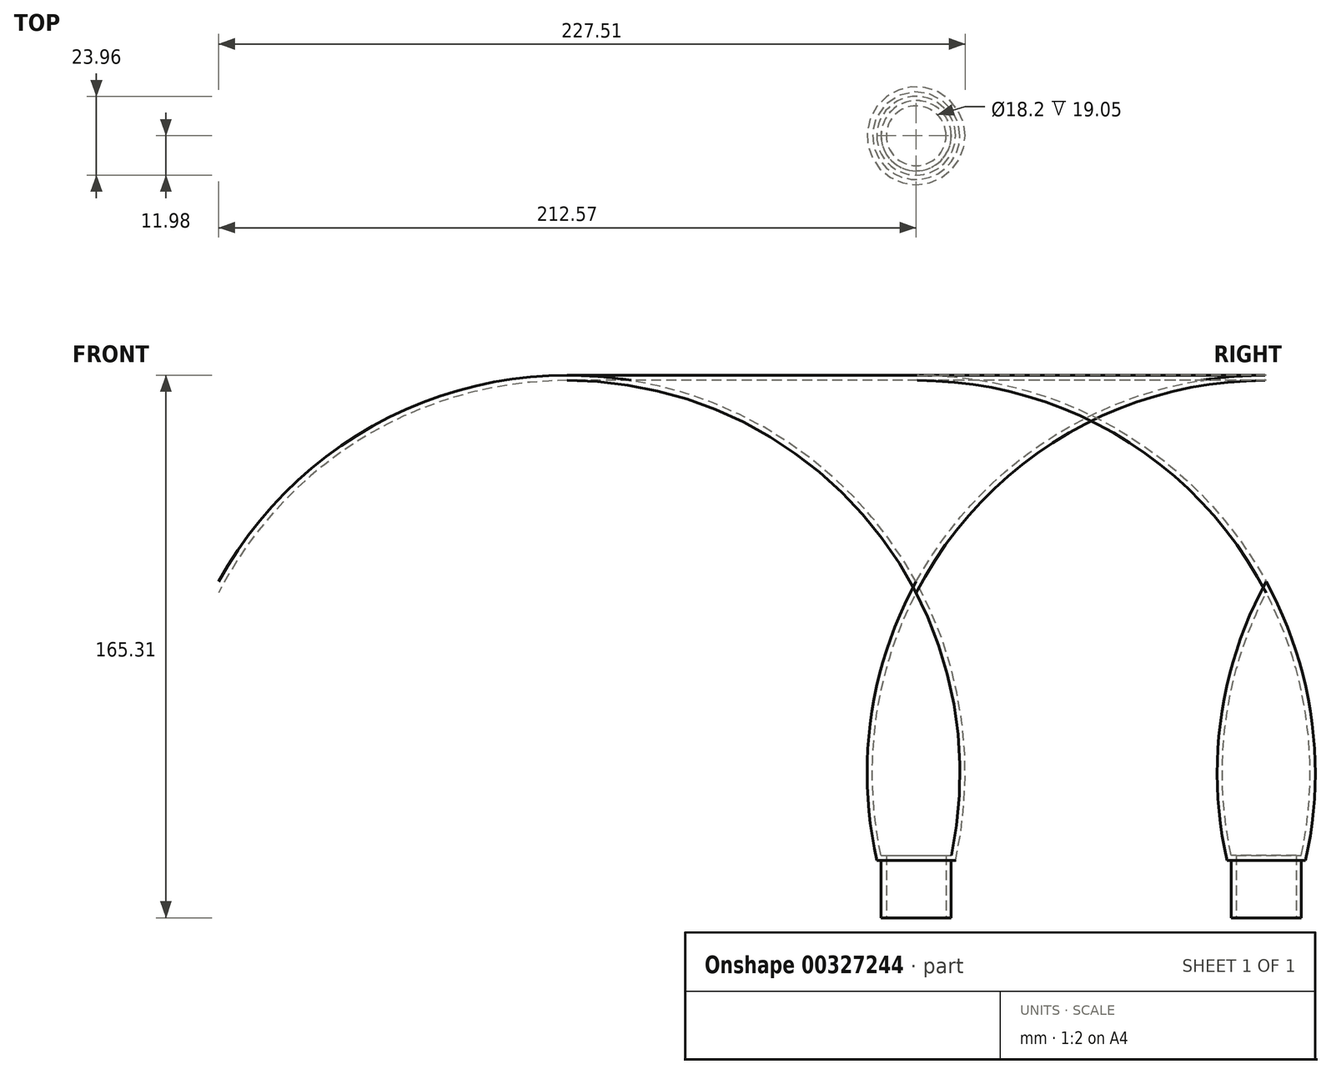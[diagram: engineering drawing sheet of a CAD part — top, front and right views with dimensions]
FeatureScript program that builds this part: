
annotation { "Feature Type Name" : "Feature", "Feature Type Description" : "" }
export const myFeature = defineFeature(function(context is Context, id is Id, definition is map)
    precondition{}
    {
        {
            var Q0;
            Q0=qCreatedBy(makeId("Front.planeOp"),FACE);
            var sketch = newSketch(context, id + "F0", { "sketchPlane" : qUnion([Q0])});
            skLineSegment(sketch, "E0", {"start": v(0, 0) * mm, "end": v(0, 99) * mm});
            skLineSegment(sketch, "E1", {"start": v(0, 0) * mm, "end": v(9.1, 0) * mm});
            skLineSegment(sketch, "E2", {"start": v(9.1, 0) * mm, "end": v(9.1, 19.05) * mm});
            skLineSegment(sketch, "E3", {"start": v(9.1, 19.05) * mm, "end": v(10.7, 19.05) * mm});
            skArc(sketch, "E4", {"start": v(10.7, 19.05) * mm, "mid": v(12.3, 59.95) * mm, "end": v(0, 99) * mm});
            skArc(sketch, "E5.0", {"start": v(11.98, 17.46) * mm, "mid": v(13.75, 61.01) * mm, "end": v(0, 102.38) * mm});
            skLineSegment(sketch, "E5.1", {"start": v(10.69, 17.46) * mm, "end": v(11.98, 17.46) * mm});
            skLineSegment(sketch, "E5.2", {"start": v(10.69, 0) * mm, "end": v(10.69, 17.46) * mm});
            skLineSegment(sketch, "E6", {"start": v(9.1, 0) * mm, "end": v(10.69, 0) * mm});
            skLineSegment(sketch, "E7", {"start": v(0, 99) * mm, "end": v(0, 102.38) * mm});
            skSolve(sketch);
        }
        {
            var Q0;
            Q0=makeQuery(id+"F0.imprint","IMPRINT",FACE,{"disambiguationData":[TD([[makeQuery(id+"F0.imprint","IMPRINT",EDGE,{"derivedFrom":sQuery(id+"F0.wireOp",EDGE,"E2")}),-1.0]])]});
            var Q1;
            Q1=sQuery(id+"F0.wireOp",EDGE,"E0");
            revolve(context, id + "F1", {"entities" : qUnion([Q0]), "axis" : qUnion([Q1]), "revolveType" : RevolveType.FULL});
        }
    });
